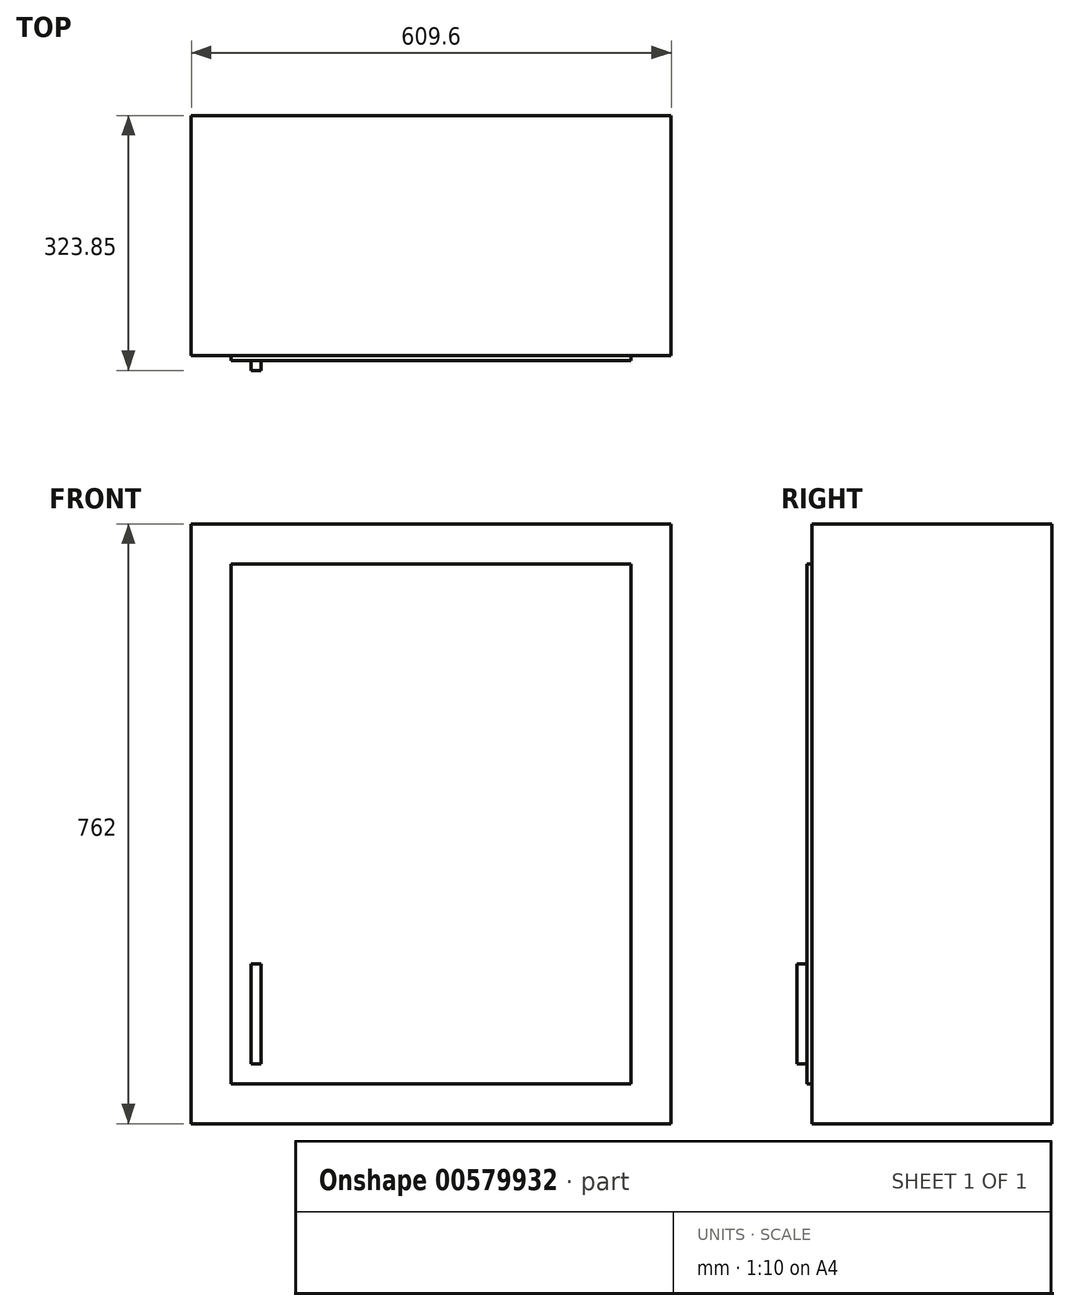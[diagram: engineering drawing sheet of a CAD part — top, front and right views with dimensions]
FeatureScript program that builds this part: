
annotation { "Feature Type Name" : "Feature", "Feature Type Description" : "" }
export const myFeature = defineFeature(function(context is Context, id is Id, definition is map)
    precondition{}
    {
        {
            var Q0;
            Q0=qCreatedBy(makeId("Front.planeOp"),FACE);
            var sketch = newSketch(context, id + "F0", { "sketchPlane" : qUnion([Q0])});
            skLineSegment(sketch, "E0.bottom", {"start": v(-324.26, 496.9) * mm, "end": v(285.34, 496.9) * mm});
            skLineSegment(sketch, "E0.top", {"start": v(-324.26, -265.1) * mm, "end": v(285.34, -265.1) * mm});
            skLineSegment(sketch, "E0.left", {"start": v(-324.26, 496.9) * mm, "end": v(-324.26, -265.1) * mm});
            skLineSegment(sketch, "E0.right", {"start": v(285.34, 496.9) * mm, "end": v(285.34, -265.1) * mm});
            skSolve(sketch);
        }
        {
            var Q0;
            Q0 = qSketchRegion(id + "F0", true);
            extrude(context, id + "F1", {"entities" : qUnion([Q0]), "depth" : 304.8 * mm, "offsetDistance" : 25.4 * mm});
        }
        {
            var Q0;
            Q0=makeQuery(id+"F1.opExtrude","CAP_FACE",FACE,{"disambiguationData":[OSD([sQuery(id+"F0.wireOp",EDGE,"E0.bottom"),sQuery(id+"F0.wireOp",EDGE,"E0.top"),sQuery(id+"F0.wireOp",EDGE,"E0.left"),sQuery(id+"F0.wireOp",EDGE,"E0.right")])],"isStart":false});
            var sketch = newSketch(context, id + "F2", { "sketchPlane" : qUnion([Q0])});
            skLineSegment(sketch, "E1.bottom", {"start": v(-273.46, 446.1) * mm, "end": v(234.54, 446.1) * mm});
            skLineSegment(sketch, "E1.top", {"start": v(-273.46, -214.3) * mm, "end": v(234.54, -214.3) * mm});
            skLineSegment(sketch, "E1.left", {"start": v(-273.46, 446.1) * mm, "end": v(-273.46, -214.3) * mm});
            skLineSegment(sketch, "E1.right", {"start": v(234.54, 446.1) * mm, "end": v(234.54, -214.3) * mm});
            skSolve(sketch);
        }
        {
            var Q0;
            Q0=makeQuery(id+"F2.imprint","IMPRINT",FACE,{"disambiguationData":[TD([[makeQuery(id+"F2.imprint","IMPRINT",EDGE,{"derivedFrom":sQuery(id+"F2.wireOp",EDGE,"E1.bottom")}),-1.0]])]});
            extrude(context, id + "F3", {"entities" : qUnion([Q0]), "operationType" : NewBodyOperationType.ADD, "depth" : 6.35 * mm, "offsetDistance" : 25.4 * mm});
        }
        {
            var Q0;
            Q0=makeQuery(id+"F3.opExtrude","CAP_FACE",FACE,{"disambiguationData":[OSD([sQuery(id+"F2.wireOp",EDGE,"E1.bottom"),sQuery(id+"F2.wireOp",EDGE,"E1.top"),sQuery(id+"F2.wireOp",EDGE,"E1.left"),sQuery(id+"F2.wireOp",EDGE,"E1.right")])],"isStart":false});
            var sketch = newSketch(context, id + "F4", { "sketchPlane" : qUnion([Q0])});
            skLineSegment(sketch, "E2.bottom", {"start": v(-248.06, -61.9) * mm, "end": v(-235.36, -61.9) * mm});
            skLineSegment(sketch, "E2.top", {"start": v(-248.06, -188.9) * mm, "end": v(-235.36, -188.9) * mm});
            skLineSegment(sketch, "E2.left", {"start": v(-248.06, -61.9) * mm, "end": v(-248.06, -188.9) * mm});
            skLineSegment(sketch, "E2.right", {"start": v(-235.36, -61.9) * mm, "end": v(-235.36, -188.9) * mm});
            skSolve(sketch);
        }
        {
            var Q0;
            Q0 = qSketchRegion(id + "F4", true);
            extrude(context, id + "F5", {"entities" : qUnion([Q0]), "operationType" : NewBodyOperationType.ADD, "depth" : 12.7 * mm, "offsetDistance" : 25.4 * mm});
        }
    });
